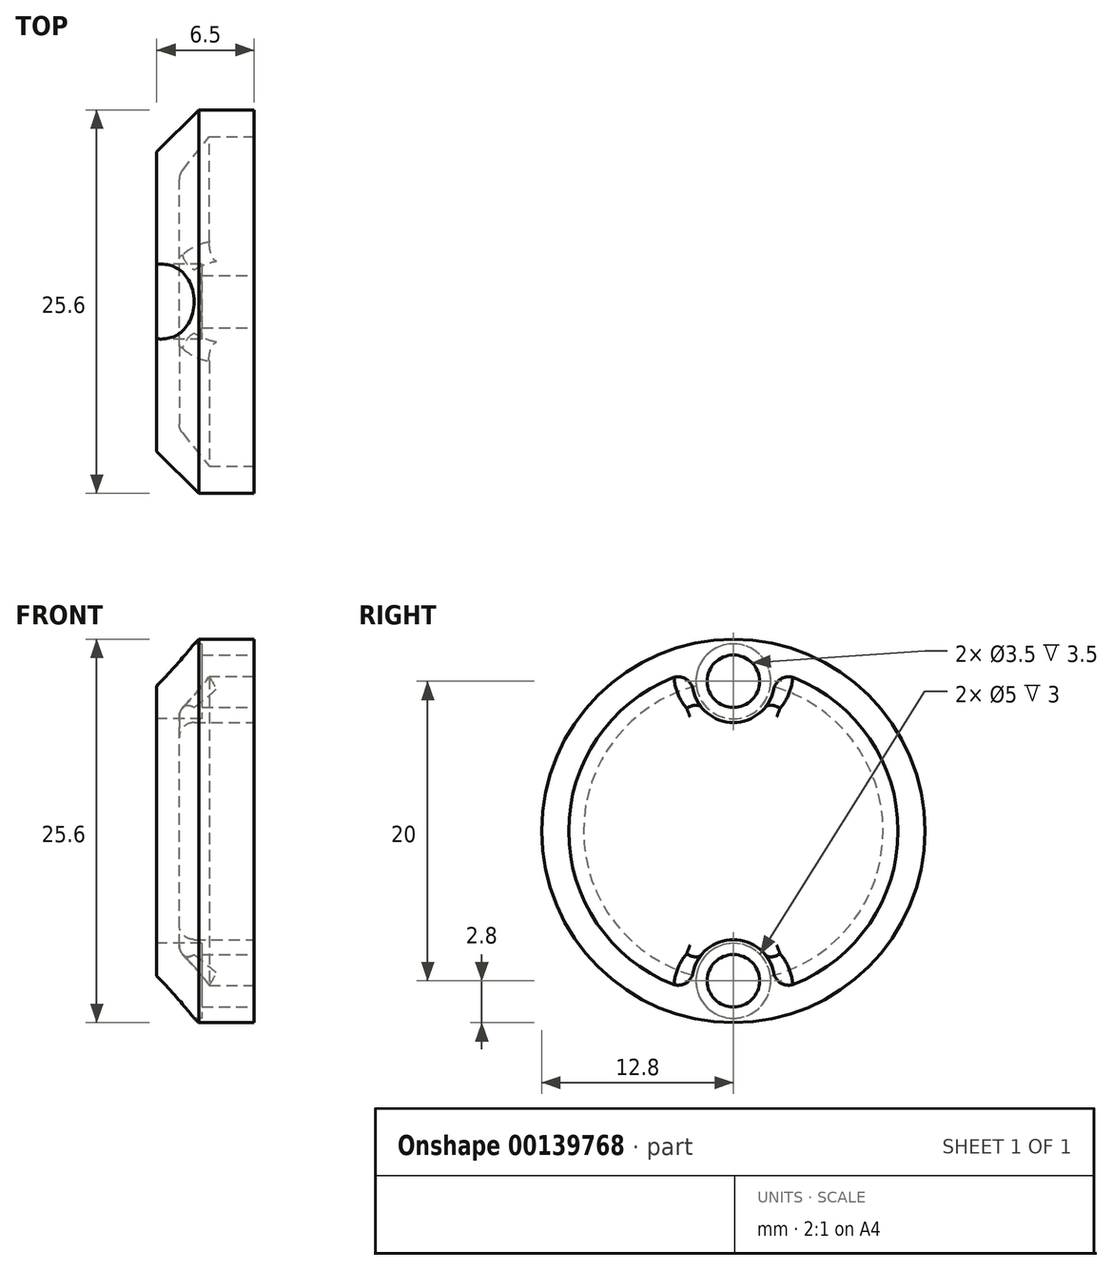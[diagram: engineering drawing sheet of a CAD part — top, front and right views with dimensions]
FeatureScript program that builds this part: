
annotation { "Feature Type Name" : "Feature", "Feature Type Description" : "" }
export const myFeature = defineFeature(function(context is Context, id is Id, definition is map)
    precondition{}
    {
        {
            var Q0;
            Q0=qCreatedBy(makeId("Front.planeOp"),FACE);
            var sketch = newSketch(context, id + "F0", { "sketchPlane" : qUnion([Q0])});
            skLineSegment(sketch, "E0", {"start": v(0, 0) * mm, "end": v(0, 12.8) * mm});
            skLineSegment(sketch, "E1", {"start": v(0, 12.8) * mm, "end": v(6.5, 12.8) * mm});
            skLineSegment(sketch, "E2", {"start": v(6.5, 12.8) * mm, "end": v(6.5, 11) * mm});
            skLineSegment(sketch, "E3", {"start": v(1.5, 8.5) * mm, "end": v(1.5, 0) * mm});
            skLineSegment(sketch, "E4", {"start": v(1.5, 0) * mm, "end": v(0, 0) * mm});
            skLineSegment(sketch, "E5", {"start": v(6.5, 11) * mm, "end": v(3.5, 11) * mm});
            skLineSegment(sketch, "E6", {"start": v(3.5, 11) * mm, "end": v(1.5, 8.5) * mm});
            skSolve(sketch);
        }
        {
            var Q0;
            Q0=makeQuery(id+"F0.imprint","IMPRINT",FACE,{"disambiguationData":[TD([[makeQuery(id+"F0.imprint","IMPRINT",EDGE,{"derivedFrom":sQuery(id+"F0.wireOp",EDGE,"E0")}),-1.0]])]});
            var Q1;
            Q1=sQuery(id+"F0.wireOp",EDGE,"E4");
            revolve(context, id + "F1", {"entities" : qUnion([Q0]), "axis" : qUnion([Q1]), "revolveType" : RevolveType.FULL});
        }
        {
            var Q0;
            Q0=makeQuery(id+"F1.opRevolve","SWEPT_FACE",FACE,{"disambiguationData":[OSD([sQuery(id+"F0.wireOp",EDGE,"E2")])]});
            var sketch = newSketch(context, id + "F2", { "sketchPlane" : qUnion([Q0])});
            skCircle(sketch, "E7", {"center": v(0, 10) * mm, "radius": 2.75 * mm});
            skCircle(sketch, "E8.MirrorC", {"center": v(0, -10) * mm, "radius": 2.75 * mm});
            skSolve(sketch);
        }
        {
            var Q0;
            Q0 = qSketchRegion(id + "F2", true);
            extrude(context, id + "F3", {"entities" : qUnion([Q0]), "operationType" : NewBodyOperationType.ADD, "oppositeDirection" : true, "depth" : 5.5 * mm});
        }
        {
            var Q0;
            Q0=qCreatedBy(makeId("Front.planeOp"),FACE);
            var sketch = newSketch(context, id + "F4", { "sketchPlane" : qUnion([Q0])});
            skLineSegment(sketch, "E9", {"start": v(-7, 0) * mm, "end": v(-7, 18.58) * mm});
            skLineSegment(sketch, "E10", {"start": v(-7, 18.58) * mm, "end": v(8.58, 18.58) * mm});
            skLineSegment(sketch, "E11", {"start": v(8.58, 18.58) * mm, "end": v(0, 10) * mm});
            skLineSegment(sketch, "E12", {"start": v(0, 10) * mm, "end": v(0, 0) * mm});
            skLineSegment(sketch, "E13", {"start": v(0, 0) * mm, "end": v(-7, 0) * mm});
            skSolve(sketch);
        }
        {
            var Q0;
            Q0=makeQuery(id+"F3.boolean.opBoolean","INTERSECT",EDGE,{"disambiguationData":[OD(0.0)],"derivedFrom":[makeQuery(id+"F1.opRevolve","SWEPT_FACE",FACE,{"disambiguationData":[OSD([sQuery(id+"F0.wireOp",EDGE,"E6")])]}),makeQuery(id+"F3.opExtrude","SWEPT_FACE",FACE,{"disambiguationData":[OSD([sQuery(id+"F2.wireOp",EDGE,"E7")])]})]});
            var Q1;
            Q1=makeQuery(id+"F3.boolean.opBoolean","INTERSECT",EDGE,{"disambiguationData":[OD(0.0)],"derivedFrom":[makeQuery(id+"F1.opRevolve","SWEPT_FACE",FACE,{"disambiguationData":[OSD([sQuery(id+"F0.wireOp",EDGE,"E5")])]}),makeQuery(id+"F3.opExtrude","SWEPT_FACE",FACE,{"disambiguationData":[OSD([sQuery(id+"F2.wireOp",EDGE,"E7")])]})]});
            var Q2;
            Q2=makeQuery(id+"F3.boolean.opBoolean","INTERSECT",EDGE,{"disambiguationData":[OD(1.0)],"derivedFrom":[makeQuery(id+"F1.opRevolve","SWEPT_FACE",FACE,{"disambiguationData":[OSD([sQuery(id+"F0.wireOp",EDGE,"E6")])]}),makeQuery(id+"F3.opExtrude","SWEPT_FACE",FACE,{"disambiguationData":[OSD([sQuery(id+"F2.wireOp",EDGE,"E7")])]})]});
            var Q3;
            Q3=makeQuery(id+"F3.boolean.opBoolean","INTERSECT",EDGE,{"disambiguationData":[OD(1.0)],"derivedFrom":[makeQuery(id+"F1.opRevolve","SWEPT_FACE",FACE,{"disambiguationData":[OSD([sQuery(id+"F0.wireOp",EDGE,"E5")])]}),makeQuery(id+"F3.opExtrude","SWEPT_FACE",FACE,{"disambiguationData":[OSD([sQuery(id+"F2.wireOp",EDGE,"E7")])]})]});
            var Q4;
            Q4=makeQuery(id+"F3.boolean.opBoolean","INTERSECT",EDGE,{"derivedFrom":[makeQuery(id+"F1.opRevolve","SWEPT_FACE",FACE,{"disambiguationData":[OSD([sQuery(id+"F0.wireOp",EDGE,"E3")])]}),makeQuery(id+"F3.opExtrude","SWEPT_FACE",FACE,{"disambiguationData":[OSD([sQuery(id+"F2.wireOp",EDGE,"E7")])]})]});
            var Q5;
            Q5=makeQuery(id+"F3.boolean.opBoolean","SPLIT",EDGE,{"disambiguationData":[OD(1.0)],"derivedFrom":makeQuery(id+"F1.opRevolve","SWEPT_EDGE",EDGE,{"disambiguationData":[OSD([sQuery(id+"F0.wireOp",EDGE,"E3"),sQuery(id+"F0.wireOp",EDGE,"E6")])]})});
            var Q6;
            Q6=makeQuery(id+"F3.boolean.opBoolean","SPLIT",EDGE,{"disambiguationData":[OD(0.0)],"derivedFrom":makeQuery(id+"F1.opRevolve","SWEPT_EDGE",EDGE,{"disambiguationData":[OSD([sQuery(id+"F0.wireOp",EDGE,"E3"),sQuery(id+"F0.wireOp",EDGE,"E6")])]})});
            var Q7;
            Q7=makeQuery(id+"F3.boolean.opBoolean","INTERSECT",EDGE,{"disambiguationData":[OD(1.0)],"derivedFrom":[makeQuery(id+"F1.opRevolve","SWEPT_FACE",FACE,{"disambiguationData":[OSD([sQuery(id+"F0.wireOp",EDGE,"E5")])]}),makeQuery(id+"F3.opExtrude","SWEPT_FACE",FACE,{"disambiguationData":[OSD([sQuery(id+"F2.wireOp",EDGE,"E8.MirrorC")])]})]});
            var Q8;
            Q8=makeQuery(id+"F3.boolean.opBoolean","INTERSECT",EDGE,{"disambiguationData":[OD(1.0)],"derivedFrom":[makeQuery(id+"F1.opRevolve","SWEPT_FACE",FACE,{"disambiguationData":[OSD([sQuery(id+"F0.wireOp",EDGE,"E6")])]}),makeQuery(id+"F3.opExtrude","SWEPT_FACE",FACE,{"disambiguationData":[OSD([sQuery(id+"F2.wireOp",EDGE,"E8.MirrorC")])]})]});
            var Q9;
            Q9=makeQuery(id+"F3.boolean.opBoolean","INTERSECT",EDGE,{"derivedFrom":[makeQuery(id+"F1.opRevolve","SWEPT_FACE",FACE,{"disambiguationData":[OSD([sQuery(id+"F0.wireOp",EDGE,"E3")])]}),makeQuery(id+"F3.opExtrude","SWEPT_FACE",FACE,{"disambiguationData":[OSD([sQuery(id+"F2.wireOp",EDGE,"E8.MirrorC")])]})]});
            var Q10;
            Q10=makeQuery(id+"F3.boolean.opBoolean","INTERSECT",EDGE,{"disambiguationData":[OD(0.0)],"derivedFrom":[makeQuery(id+"F1.opRevolve","SWEPT_FACE",FACE,{"disambiguationData":[OSD([sQuery(id+"F0.wireOp",EDGE,"E6")])]}),makeQuery(id+"F3.opExtrude","SWEPT_FACE",FACE,{"disambiguationData":[OSD([sQuery(id+"F2.wireOp",EDGE,"E8.MirrorC")])]})]});
            var Q11;
            Q11=makeQuery(id+"F3.boolean.opBoolean","INTERSECT",EDGE,{"disambiguationData":[OD(0.0)],"derivedFrom":[makeQuery(id+"F1.opRevolve","SWEPT_FACE",FACE,{"disambiguationData":[OSD([sQuery(id+"F0.wireOp",EDGE,"E5")])]}),makeQuery(id+"F3.opExtrude","SWEPT_FACE",FACE,{"disambiguationData":[OSD([sQuery(id+"F2.wireOp",EDGE,"E8.MirrorC")])]})]});
            fillet(context, id + "F5", {"entities" : qUnion([Q0, Q1, Q2, Q3, Q4, Q5, Q6, Q7, Q8, Q9, Q10, Q11]), "radius" : 1 * mm, "tangentPropagation" : true, "allowEdgeOverflow" : false});
        }
        {
            var Q0;
            Q0=makeQuery(id+"F4.imprint","IMPRINT",FACE,{"disambiguationData":[TD([[makeQuery(id+"F4.imprint","IMPRINT",EDGE,{"derivedFrom":sQuery(id+"F4.wireOp",EDGE,"E9")}),-1.0]])]});
            var Q1;
            Q1=makeQuery(id+"F3.boolean.opBoolean","SPLIT",FACE,{"disambiguationData":[OD(0.0)],"derivedFrom":makeQuery(id+"F1.opRevolve","SWEPT_FACE",FACE,{"disambiguationData":[OSD([sQuery(id+"F0.wireOp",EDGE,"E5")])]})});
            revolve(context, id + "F6", {"operationType" : NewBodyOperationType.REMOVE, "entities" : qUnion([Q0]), "axis" : qUnion([Q1]), "revolveType" : RevolveType.FULL, "oppositeDirection" : true});
        }
        {
            var Q0;
            Q0=makeQuery(id+"F3.boolean.opBoolean","MERGE",FACE,{"derivedFrom":[makeQuery(id+"F1.opRevolve","SWEPT_FACE",FACE,{"disambiguationData":[OSD([sQuery(id+"F0.wireOp",EDGE,"E2")])]}),makeQuery(id+"F3.opExtrude","CAP_FACE",FACE,{"disambiguationData":[OSD([sQuery(id+"F2.wireOp",EDGE,"E7")])],"isStart":true}),makeQuery(id+"F3.opExtrude","CAP_FACE",FACE,{"disambiguationData":[OSD([sQuery(id+"F2.wireOp",EDGE,"E8.MirrorC")])],"isStart":true})]});
            var sketch = newSketch(context, id + "F7", { "sketchPlane" : qUnion([Q0])});
            skPoint(sketch, "E14", {"position": v(0, -10) * mm});
            skPoint(sketch, "E15", {"position": v(0, 10) * mm});
            skCircle(sketch, "E16", {"center": v(0, -10) * mm, "radius": 1.75 * mm});
            skCircle(sketch, "E17", {"center": v(0, 10) * mm, "radius": 1.75 * mm});
            skSolve(sketch);
        }
        {
            var Q0;
            Q0=makeQuery(id+"F7.imprint","IMPRINT",FACE,{"disambiguationData":[TD([[makeQuery(id+"F7.imprint","IMPRINT",EDGE,{"derivedFrom":sQuery(id+"F7.wireOp",EDGE,"E16")}),1.0]])]});
            var Q1;
            Q1=makeQuery(id+"F7.imprint","IMPRINT",FACE,{"disambiguationData":[TD([[makeQuery(id+"F7.imprint","IMPRINT",EDGE,{"derivedFrom":sQuery(id+"F7.wireOp",EDGE,"E17")}),1.0]])]});
            extrude(context, id + "F8", {"entities" : qUnion([Q0, Q1]), "operationType" : NewBodyOperationType.REMOVE, "oppositeDirection" : true, "depth" : 25 * mm});
        }
        {
            var Q0;
            Q0=makeQuery(id+"F1.opRevolve","SWEPT_FACE",FACE,{"disambiguationData":[OSD([sQuery(id+"F0.wireOp",EDGE,"E0")])]});
            var sketch = newSketch(context, id + "F9", { "sketchPlane" : qUnion([Q0])});
            skCircle(sketch, "E18", {"center": v(0, 10) * mm, "radius": 2.5 * mm});
            skCircle(sketch, "E19", {"center": v(0, -10) * mm, "radius": 2.5 * mm});
            skSolve(sketch);
        }
        {
            var Q0;
            {var subQ6=makeQuery(id+"F8.boolean.opBoolean","INTERSECT",EDGE,{"derivedFrom":[makeQuery(id+"F1.opRevolve","SWEPT_FACE",FACE,{"disambiguationData":[OSD([sQuery(id+"F0.wireOp",EDGE,"E0")])]}),makeQuery(id+"F8.opExtrude","SWEPT_FACE",FACE,{"disambiguationData":[OSD([sQuery(id+"F7.wireOp",EDGE,"E17")])]})]});Q0=makeQuery(id+"F9.imprint","IMPRINT",FACE,{"disambiguationData":[TD([[makeQuery(id+"F9.imprint","IMPRINT",EDGE,{"derivedFrom":subQ6}),1.0]])]});}
            var Q1;
            {var subQ6=makeQuery(id+"F8.boolean.opBoolean","INTERSECT",EDGE,{"derivedFrom":[makeQuery(id+"F1.opRevolve","SWEPT_FACE",FACE,{"disambiguationData":[OSD([sQuery(id+"F0.wireOp",EDGE,"E0")])]}),makeQuery(id+"F8.opExtrude","SWEPT_FACE",FACE,{"disambiguationData":[OSD([sQuery(id+"F7.wireOp",EDGE,"E17")])]})]});Q1=makeQuery(id+"F9.imprint","IMPRINT",FACE,{"disambiguationData":[TD([[makeQuery(id+"F9.imprint","IMPRINT",EDGE,{"derivedFrom":subQ6}),-1.0]])]});}
            var Q2;
            {var subQ6=makeQuery(id+"F8.boolean.opBoolean","INTERSECT",EDGE,{"derivedFrom":[makeQuery(id+"F1.opRevolve","SWEPT_FACE",FACE,{"disambiguationData":[OSD([sQuery(id+"F0.wireOp",EDGE,"E0")])]}),makeQuery(id+"F8.opExtrude","SWEPT_FACE",FACE,{"disambiguationData":[OSD([sQuery(id+"F7.wireOp",EDGE,"E16")])]})]});Q2=makeQuery(id+"F9.imprint","IMPRINT",FACE,{"disambiguationData":[TD([[makeQuery(id+"F9.imprint","IMPRINT",EDGE,{"derivedFrom":subQ6}),1.0]])]});}
            var Q3;
            {var subQ6=makeQuery(id+"F8.boolean.opBoolean","INTERSECT",EDGE,{"derivedFrom":[makeQuery(id+"F1.opRevolve","SWEPT_FACE",FACE,{"disambiguationData":[OSD([sQuery(id+"F0.wireOp",EDGE,"E0")])]}),makeQuery(id+"F8.opExtrude","SWEPT_FACE",FACE,{"disambiguationData":[OSD([sQuery(id+"F7.wireOp",EDGE,"E16")])]})]});Q3=makeQuery(id+"F9.imprint","IMPRINT",FACE,{"disambiguationData":[TD([[makeQuery(id+"F9.imprint","IMPRINT",EDGE,{"derivedFrom":subQ6}),-1.0]])]});}
            extrude(context, id + "F10", {"entities" : qUnion([Q0, Q1, Q2, Q3]), "operationType" : NewBodyOperationType.REMOVE, "oppositeDirection" : true, "depth" : 3 * mm});
        }
    });
